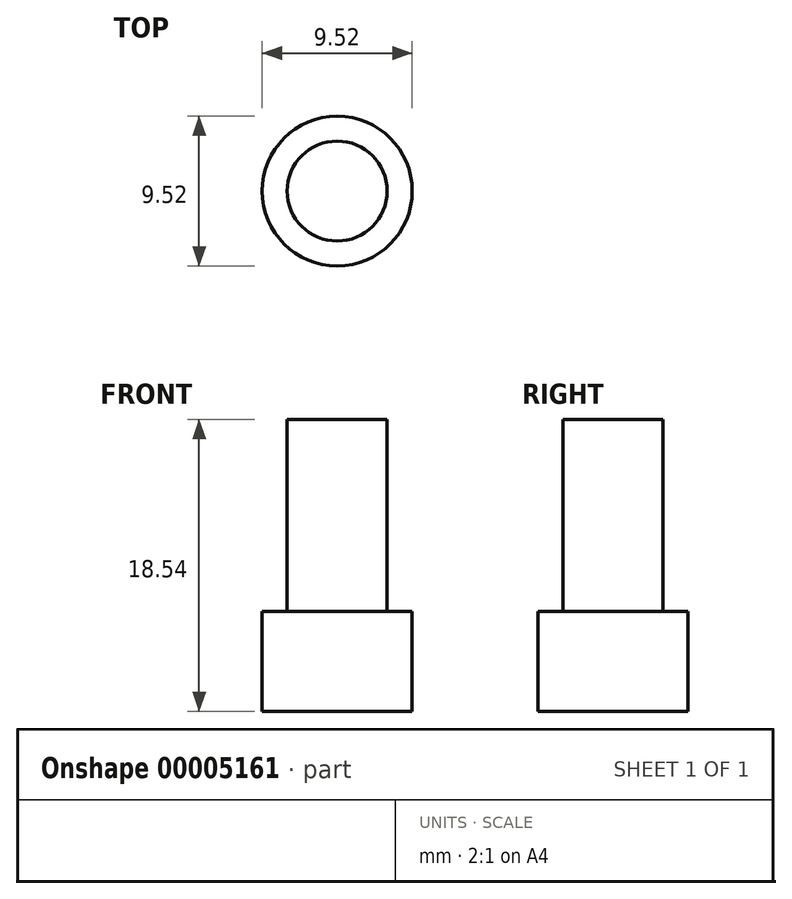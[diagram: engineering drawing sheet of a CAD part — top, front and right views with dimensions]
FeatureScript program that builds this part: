
annotation { "Feature Type Name" : "Feature", "Feature Type Description" : "" }
export const myFeature = defineFeature(function(context is Context, id is Id, definition is map)
    precondition{}
    {
        {
            var Q0;
            Q0=qCreatedBy(makeId("Top.planeOp"),FACE);
            var sketch = newSketch(context, id + "F0", { "sketchPlane" : qUnion([Q0])});
            skCircle(sketch, "E0", {"center": v(0, 0) * mm, "radius": 4.76 * mm});
            skCircle(sketch, "E1", {"center": v(0, 0) * mm, "radius": 3.18 * mm});
            skSolve(sketch);
        }
        {
            var Q0;
            Q0=makeQuery(id+"F0.imprint","IMPRINT",FACE,{"disambiguationData":[TD([[makeQuery(id+"F0.imprint","IMPRINT",EDGE,{"derivedFrom":sQuery(id+"F0.wireOp",EDGE,"E1")}),1.0]])]});
            extrude(context, id + "F1", {"entities" : qUnion([Q0]), "depth" : 18.54 * mm});
        }
        {
            var Q0;
            Q0=makeQuery(id+"F0.imprint","IMPRINT",FACE,{"disambiguationData":[TD([[makeQuery(id+"F0.imprint","IMPRINT",EDGE,{"derivedFrom":sQuery(id+"F0.wireOp",EDGE,"E0")}),1.0]])]});
            extrude(context, id + "F2", {"entities" : qUnion([Q0]), "operationType" : NewBodyOperationType.ADD, "depth" : 6.35 * mm});
        }
    });
